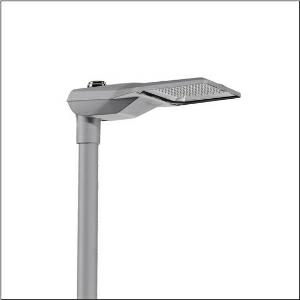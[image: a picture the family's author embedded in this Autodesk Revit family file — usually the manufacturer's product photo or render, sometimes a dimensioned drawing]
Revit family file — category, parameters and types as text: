
# Revit family: streetlight_sl_21_midi___st1_0a_5xe7d47n08lb_f0d9
name_source: partatom
category: Lighting Fixtures
units: mm (PartAtom-declared; Revit-internal decimal feet)

## family parameters
Cut with Voids When Loaded = No
Host = Face
Light Source = No
Part Type = Normal
Room Calculation Point = No
Round Connector Dimension = Use Diameter
Shared = No

## types (1)
- --- (1 x LED, 14950 lm, 98.3 W, 4000K)
    Apparent Load = 98 VA
    CIE Flux Codes = 37 72 97 100 100
    Color Rendering = 70
    Color Temperature = 4000K
    Default Elevation = 1800 mm
    Description = Streetlight SL 21 midi, mast luminaire, primary light control with lens, of PMMA, primary optical cover: cover, of toughened safety glass, transparent, light distribution: ST1.0a, light emission: direct distribution, primary light characteristic: asymmetric, installation type: side-entry, LED, 3G 2.5mm², High Power LED, rated luminous flux: 14.950lm, luminous efficacy: 152lm/W, light colour: 740, colour temperature: 4000K, control gear: NEMA (7pin), control: overheat protection, pre-setting: linear dimming characteristic, constant luminous flux control, time-dependent luminous flux control, flexible luminous flux parameterisation, mains connection: 220..240V, AC, 50/60Hz, connection cable pre-assembled, cable length: 10,5m, wiring characteristics: H05VV-F, start of lifetime: 98W, end of service life: 101W, reduction: 45W, luminaire housing, of diecast aluminium (EN AC-44300), powder-coated, Siteco® metallic grey (DB 702S), corrosivity category C5 mid according to DIN EN ISO 12944, multi-level sealing system, sealing non-destructively replaceable, inclination adjustable: 0°, 5°, 10°, 15°, length: 644mm, width: 335mm, height: 110mm, spigot size: 42mm (side-entry), mounting height: 4..8m, protection rating (complete): IP66, insulation class (complete): insulation class I (protective earthing), certification: CE, ENEC, ENEC+, VDE, impact resistance: IK10, permissible operating ambient temperature for outdoor applications: -40..+50°C, standard-compliant lighting for roads and squares, packaging unit: 1 piece

Light Distribution: ST1.0a
    Height = 111 mm
    Lamp = 1 x LED
    Lamp Light Flux = 14950 lm
    Lamp Power = 98.3 W
    Lamp count = 1
    Length = 644 mm
    Luminous efficacy = 152 lm/W
    Manufacturer = Siteco
    ModVariant = No
    Model = 5XE7D47N08LB
    Number of Poles = 1
    OnlyDefault = Yes
    Power Factor = 1
    Product Name = Streetlight SL 21 midi | ST1.0a
    Product group = mast luminaire | pylon top
    ProductGroupID = 6100
    Protection Class = Protection class I
    Protection Degree = IP 66
    RLX_Detail_Level = 1
    RLX_Emergency_Light_Flux = 0 lm
    RLX_Emergency_Type = 0
    RLX_Emergency_Type_DB = No
    RlxData = <blob elided: 26689 chars, md5=89742694>
    Socket = socket
    Standby Power = 0 W
    System Light Flux = 14950 lm
    System Power = 98 W
    Type Comments = factory setting: luminous flux: 100 % | dim-lin: 254 | 1020 mA
    Type Image = l_1294377.jpg
    URL = http://relux.com
    VarID = @adj_157487
    Voltage = 0 V
    Weight = 0.00 kg
    Width = 336 mm

## geometry (parser evidence)
native form markers: Blend x4, Sweep x11
no freeform markers — native parametric forms only
